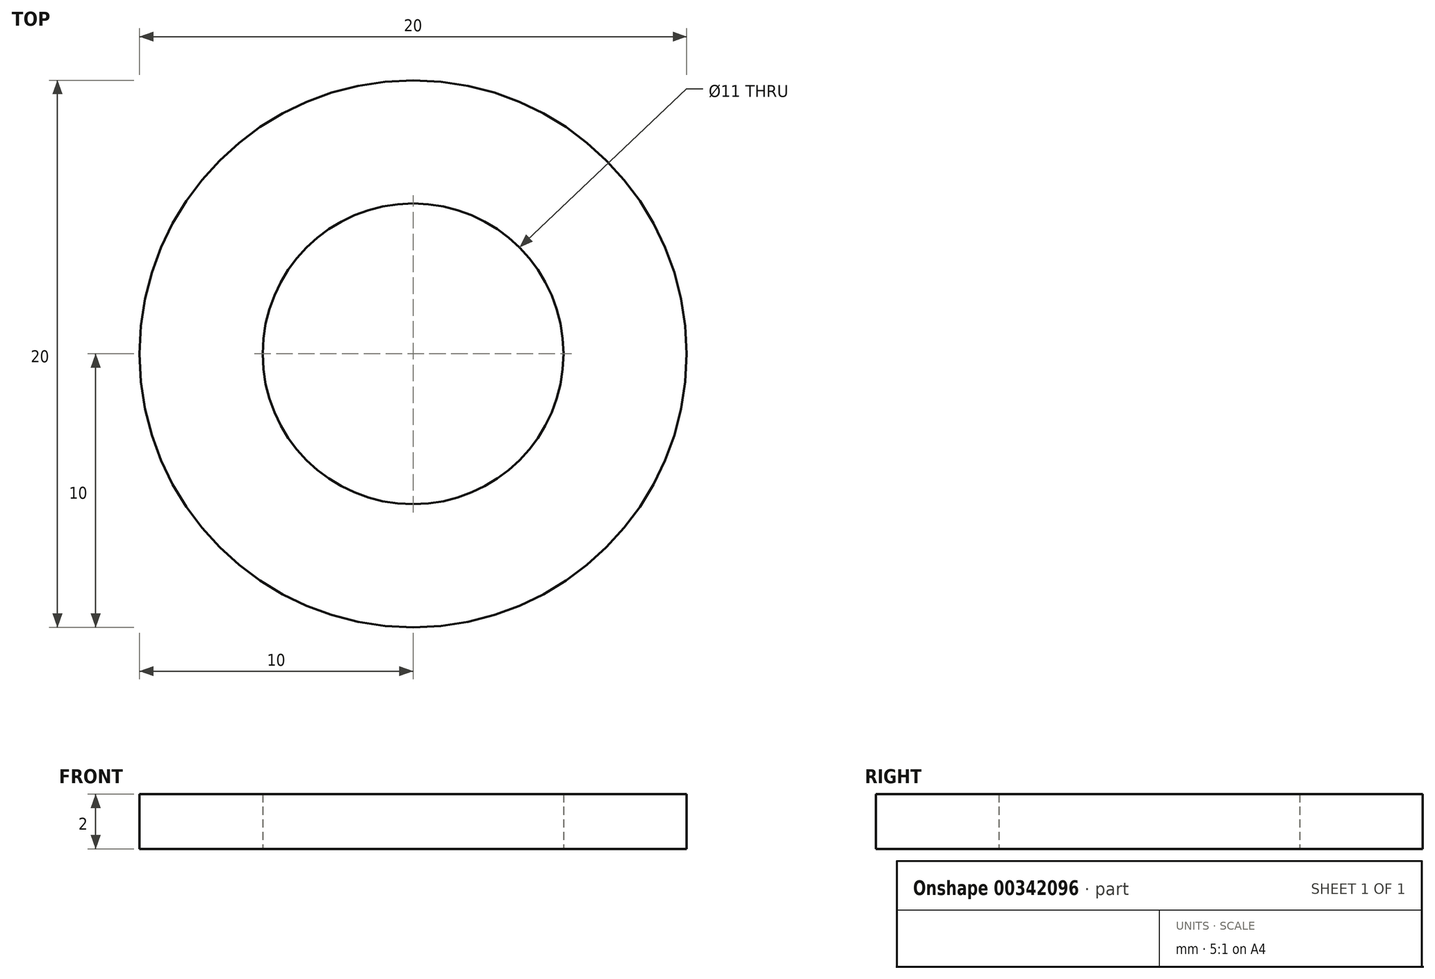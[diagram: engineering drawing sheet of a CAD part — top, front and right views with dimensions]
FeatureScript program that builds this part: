
annotation { "Feature Type Name" : "Feature", "Feature Type Description" : "" }
export const myFeature = defineFeature(function(context is Context, id is Id, definition is map)
    precondition{}
    {
        {
            var Q0;
            Q0=qCreatedBy(makeId("Top.planeOp"),FACE);
            var sketch = newSketch(context, id + "F0", { "sketchPlane" : qUnion([Q0])});
            skCircle(sketch, "E0", {"center": v(0, 0) * mm, "radius": 10 * mm});
            skCircle(sketch, "E1", {"center": v(0, 0) * mm, "radius": 5.5 * mm});
            skSolve(sketch);
        }
        {
            var Q0;
            Q0=qSketchRegion(id+"F0",true);
            var Q1;
            Q1=makeQuery(id+"F0.imprint","IMPRINT",FACE,{"disambiguationData":[TD([[makeQuery(id+"F0.imprint","IMPRINT",EDGE,{"derivedFrom":sQuery(id+"F0.wireOp",EDGE,"E0")}),1.0]])]});
            extrude(context, id + "F1", {"entities" : qUnion([Q0, Q1]), "depth" : 2 * mm});
        }
    });
